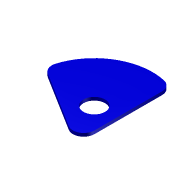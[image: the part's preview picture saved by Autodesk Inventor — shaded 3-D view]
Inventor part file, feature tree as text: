
AUTODESK INVENTOR PART (.ipt)
format: ipt  version: 2012 (Build 160160000, 160)  size: 87,552 bytes
history: native  units: mm
features: extrude x1, sketch x1
ambient origin geometry x8: Origin, YZ Plane, XZ Plane, XY Plane, X Axis, Y Axis, Z Axis, Center Point
feature tree (2):
  extrude  "Extrusion5"  Depth=54.0mm
  sketch  "Sketch1"  dims[d0=108.0mm d14=54.0mm d21=8.0mm d25=54.0mm d28=10.12291mm d30=20.0mm d33=21.515487mm d38=10.0mm d41=3.0mm d42=0.0mm]
